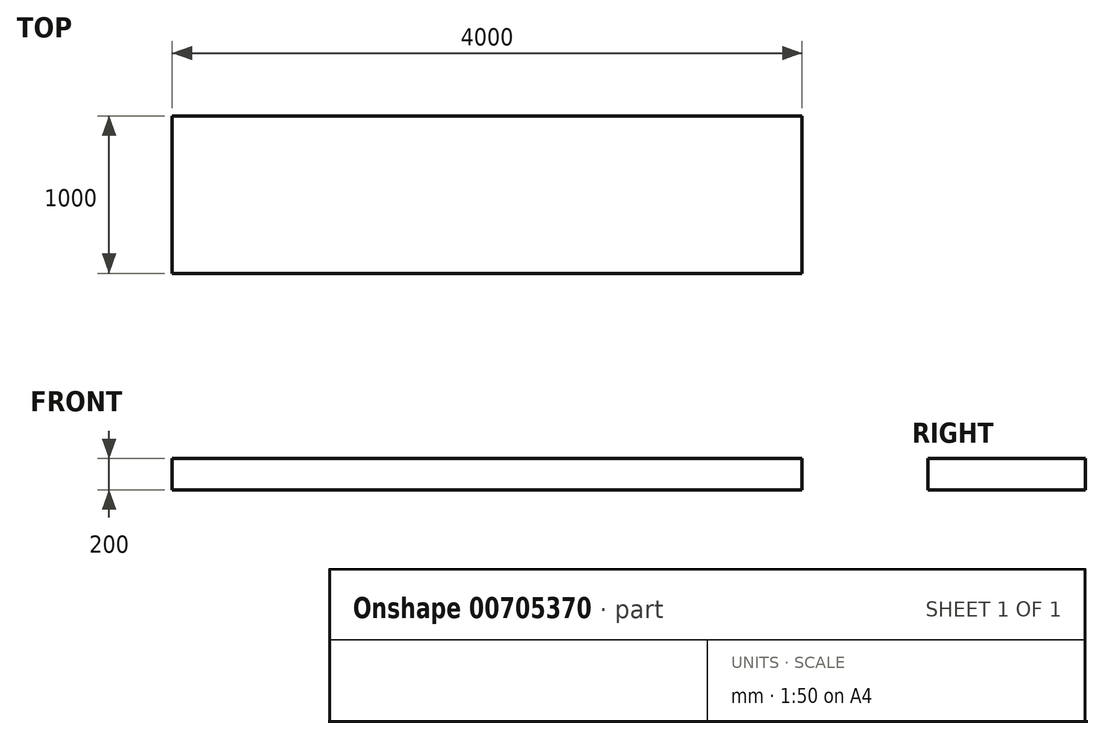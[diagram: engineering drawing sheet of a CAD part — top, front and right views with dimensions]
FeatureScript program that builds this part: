
annotation { "Feature Type Name" : "Feature", "Feature Type Description" : "" }
export const myFeature = defineFeature(function(context is Context, id is Id, definition is map)
    precondition{}
    {
        {
            var Q0;
            Q0=qCreatedBy(makeId("Top.planeOp"),FACE);
            var sketch = newSketch(context, id + "F0", { "sketchPlane" : qUnion([Q0])});
            skLineSegment(sketch, "E0.bottom", {"start": v(2000, 500) * mm, "end": v(-2000, 500) * mm});
            skLineSegment(sketch, "E0.top", {"start": v(2000, -500) * mm, "end": v(-2000, -500) * mm});
            skLineSegment(sketch, "E0.left", {"start": v(2000, 500) * mm, "end": v(2000, -500) * mm});
            skLineSegment(sketch, "E0.right", {"start": v(-2000, 500) * mm, "end": v(-2000, -500) * mm});
            skPoint(sketch, "E0.middle", {"position": v(0, 0) * mm});
            skSolve(sketch);
        }
        {
            var Q0;
            Q0=makeQuery(id+"F0.imprint","IMPRINT",FACE,{"disambiguationData":[TD([[makeQuery(id+"F0.imprint","IMPRINT",EDGE,{"derivedFrom":sQuery(id+"F0.wireOp",EDGE,"E0.bottom")}),1.0]])]});
            extrude(context, id + "F1", {"entities" : qUnion([Q0]), "depth" : 100 * mm, "offsetDistance" : 25.4 * mm});
        }
        {
            var Q0;
            Q0 = qSketchRegion(id + "F0", true);
            extrude(context, id + "F2", {"entities" : qUnion([Q0]), "operationType" : NewBodyOperationType.ADD, "depth" : -100 * mm, "offsetDistance" : 25.4 * mm});
        }
    });
